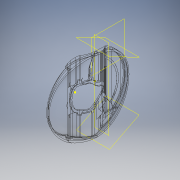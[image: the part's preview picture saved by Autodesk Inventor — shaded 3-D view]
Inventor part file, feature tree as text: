
AUTODESK INVENTOR PART (.ipt)
format: ipt  version: 2018 (Build 220112000, 112)  size: 2,382,336 bytes
history: native  units: mm
features: sketch x65, extrude x58, fillet x14, plane x4, revolve x1, mirror x1
ambient origin geometry x8: Origin, YZ Plane, XZ Plane, XY Plane, X Axis, Y Axis, Z Axis, Center Point
bodies: Solid1 (feature_tree)
feature tree (143):
  extrude  "Extrusion1"  TaperAngle=0.0deg  [1 undecoded]
  extrude  "Extrusion2"  Depth=10.0mm TaperAngle=0.0deg
  extrude  "Extrusion3"  Depth=10.0mm
  extrude  "Extrusion4"  TaperAngle=0.0deg  [1 undecoded]
  extrude  "Extrusion5"  Depth=10.0mm TaperAngle=0.0deg
  sketch  "Sketch6"  dims[d19=10.0mm d20=0.0mm d21=40.0mm]
  extrude  "Extrusion6"  Depth=10.0mm
  extrude  "Extrusion7"  Depth=11.0mm TaperAngle=0.0deg
  extrude  "Extrusion8"  Depth=32.0mm TaperAngle=0.0deg
  extrude  "Extrusion9"  Depth=32.0mm TaperAngle=0.0deg
  extrude  "Extrusion10"  Depth=10.0mm TaperAngle=0.0deg
  extrude  "Extrusion11"  Depth=10.0mm TaperAngle=0.0deg
  extrude  "Extrusion12"  TaperAngle=0.0deg  [1 undecoded]
  extrude  "Extrusion14"  Depth=48.3mm
  extrude  "Extrusion15"  TaperAngle=0.0deg  [1 undecoded]
  extrude  "Extrusion16"  Depth=10.0mm TaperAngle=0.0deg
  extrude  "Extrusion17"  Depth=11.63mm TaperAngle=0.0deg
  sketch  "Sketch21"  dims[d83=0.0mm d84=0.0mm d85=0.0mm d86=0.0mm]
  extrude  "Extrusion19"  Depth=11.63mm TaperAngle=0.0deg
  extrude  "Extrusion20"  TaperAngle=0.0deg  [1 undecoded]
  extrude  "Extrusion21"  Depth=10.0mm TaperAngle=0.0deg
  extrude  "Extrusion22"  TaperAngle=0.0deg  [1 undecoded]
  extrude  "Extrusion23"  Depth=2.86mm TaperAngle=0.0deg
  extrude  "Extrusion24"  TaperAngle=0.0deg  [1 undecoded]
  extrude  "Extrusion25"  Depth=2.22mm
  sketch  "Sketch33"  dims[d113=7.8mm d114=0.0mm d115=7.8mm d116=0.0mm]
  extrude  "Extrusion26"  Depth=10.0mm TaperAngle=0.0deg
  extrude  "Extrusion27"  Depth=7.8mm TaperAngle=0.0deg
  extrude  "Extrusion28"  Depth=16.0mm TaperAngle=0.0deg
  extrude  "Extrusion29"  Depth=22.0mm TaperAngle=0.0deg
  extrude  "Extrusion30"  Depth=17.0mm TaperAngle=0.0deg
  extrude  "Extrusion31"  Depth=2.0mm
  extrude  "Extrusion32"  Depth=2.0mm TaperAngle=0.0deg
  extrude  "Extrusion33"  Depth=18.0mm TaperAngle=0.0deg
  sketch  "Sketch42"  dims[d145=2.0mm d146=7.72mm d147=0.0mm]
  extrude  "Extrusion34"  Depth=16.0mm
  extrude  "Extrusion36"  Depth=15.5mm TaperAngle=0.0deg
  extrude  "Extrusion37"  Depth=2.0mm TaperAngle=0.0deg
  revolve  "Revolution3"  [1 undecoded]
  extrude  "Extrusion38"  Depth=2.0mm
  extrude  "Extrusion39"  Depth=2.0mm
  extrude  "Extrusion40"  Depth=2.0mm
  fillet  "Fillet1"  Radius=2.0mm
  fillet  "Fillet2"  Radius=10.0mm
  sketch  "Sketch51"
  extrude  "Extrusion41"  Depth=20.0mm TaperAngle=0.0deg
  mirror  "Mirror1"
  extrude  "Extrusion42"  [1 undecoded]
  sketch  "Sketch54"
  sketch  "Sketch55"
  sketch  "Sketch56"
  extrude  "Extrusion44"  [1 undecoded]
  extrude  "Extrusion45"  [1 undecoded]
  extrude  "Extrusion46"  [1 undecoded]
  extrude  "Extrusion47"  [1 undecoded]
  plane  "Work Plane2"
  extrude  "Extrusion48"  [1 undecoded]
  extrude  "Extrusion49"  [1 undecoded]
  plane  "Work Plane4"
  sketch  "Sketch64"
  plane  "Work Plane5"
  extrude  "Extrusion50"  [1 undecoded]
  extrude  "Extrusion51"  [1 undecoded]
  fillet  "Fillet3"  [1 undecoded]
  fillet  "Fillet4"  [1 undecoded]
  extrude  "Extrusion52"  [1 undecoded]
  extrude  "Extrusion53"  [1 undecoded]
  extrude  "Extrusion54"  [1 undecoded]
  extrude  "Extrusion55"  [1 undecoded]
  fillet  "Fillet5"  [1 undecoded]
  extrude  "Extrusion56"  [1 undecoded]
  extrude  "Extrusion57"  [1 undecoded]
  fillet  "Fillet6"  [1 undecoded]
  extrude  "Extrusion58"  [1 undecoded]
  extrude  "Extrusion59"  [1 undecoded]
  fillet  "Fillet7"  [1 undecoded]
  fillet  "Fillet8"  [1 undecoded]
  fillet  "Fillet9"  [1 undecoded]
  fillet  "Fillet10"  [1 undecoded]
  fillet  "Fillet11"  [1 undecoded]
  fillet  "Fillet12"  [1 undecoded]
  fillet  "Fillet13"  [1 undecoded]
  fillet  "Fillet14"  [1 undecoded]
  extrude  "Extrusion60"  [1 undecoded]
  extrude  "Extrusion61"  [1 undecoded]
  extrude  "Extrusion62"  [1 undecoded]
  sketch  "Sketch1"  dims[d0=10.0mm d1=0.0mm d2=0.0mm d3=0.0mm]
  sketch  "Sketch2"  dims[d4=0.0mm d5=0.0mm d6=10.0mm d7=0.0mm]
  sketch  "Sketch3"  dims[d8=10.0mm d9=0.0mm d10=50.0mm]
  sketch  "Sketch4"  dims[d11=10.0mm d12=0.0mm d13=0.0mm d14=0.0mm]
  sketch  "Sketch5"  dims[d15=0.0mm d16=0.0mm d17=10.0mm d18=0.0mm]
  sketch  "Sketch7"  dims[d22=38.0mm d23=11.0mm d24=0.0mm]
  sketch  "Sketch8"  dims[d25=9.5mm d26=0.0mm d33=32.0mm d34=0.0mm]
  sketch  "Sketch9"  dims[d37=32.0mm d38=0.0mm d39=32.0mm d40=0.0mm]
  sketch  "Sketch10"  dims[d41=32.0mm d42=0.0mm d45=10.0mm d46=0.0mm]
  sketch  "Sketch11"  dims[d47=10.0mm d48=0.0mm d49=10.0mm d50=0.0mm]
  sketch  "Sketch12"  dims[d51=0.0mm d52=0.0mm d53=0.0mm d54=0.0mm]
  sketch  "Sketch13"  dims[d65=46.0mm d66=48.3mm]
  sketch  "Sketch16"  dims[d67=9.0mm d68=0.0mm d69=0.0mm d70=0.0mm]
  sketch  "Sketch18"  dims[d71=0.0mm d72=0.0mm d73=10.0mm d74=0.0mm]
  sketch  "Sketch19"  dims[d75=5.0mm d76=0.0mm d77=11.63mm d78=0.0mm]
  sketch  "Sketch20"  dims[d79=11.63mm d80=0.0mm d81=11.63mm d82=0.0mm]
  sketch  "Sketch22"  dims[d87=30.0mm d88=10.0mm d89=0.0mm]
  sketch  "Sketch23"  dims[d92=10.0mm d93=0.0mm d94=0.0mm d95=0.0mm]
  sketch  "Sketch24"  dims[d96=135.0deg d99=2.86mm d100=0.0mm]
  sketch  "Sketch25"  dims[d101=0.0mm d102=0.0mm d103=0.0mm d104=0.0mm]
  sketch  "Sketch31"  dims[d105=2.01mm d106=2.22mm]
  sketch  "Sketch32"  dims[d107=10.0mm d108=0.0mm d109=10.0mm d110=0.0mm]
  sketch  "Sketch34"  dims[d117=0.0mm d118=0.0mm d119=16.0mm d120=0.0mm]
  sketch  "Sketch35"  dims[d121=22.0mm d122=0.0mm d123=22.0mm d124=0.0mm]
  sketch  "Sketch36"  dims[d125=90.0deg d126=17.0mm d127=0.0mm]
  sketch  "Sketch37"  dims[d128=17.0mm d129=0.0mm d130=2.0mm]
  sketch  "Sketch38"  dims[d131=2.0mm d132=6.95mm d133=0.0mm]
  sketch  "Sketch39"  dims[d134=6.95mm d135=0.0mm d136=18.0mm d137=0.0mm]
  sketch  "Sketch40"  dims[d138=16.0mm d139=0.0mm d140=1.02mm]
  sketch  "Sketch41"  dims[d141=1.0mm d142=0.0mm d143=15.5mm d144=0.0mm]
  sketch  "Sketch43"  dims[d148=17.0mm d149=0.0mm d150=2.0mm]
  sketch  "Sketch45"  dims[d151=2.0mm d152=2.0mm]
  sketch  "Sketch47"  dims[d153=2.0mm d154=2.0mm]
  sketch  "Sketch48"  dims[d155=2.0mm d156=2.0mm d157=2.0mm d158=10.0mm d159=0.0mm]
  sketch  "Sketch49"  dims[d160=7.83mm d161=0.0mm d162=20.0mm d163=0.0mm]
  sketch  "Sketch50"
  sketch  "Sketch52"
  sketch  "Sketch53"
  sketch  "Sketch57"
  sketch  "Sketch60"
  sketch  "Sketch61"
  sketch  "Sketch62"
  sketch  "Sketch63"
  plane  "Work Plane3"
  sketch  "Sketch65"
  sketch  "Sketch66"
  sketch  "Sketch67"
  sketch  "Sketch68"
  sketch  "Sketch69"
  sketch  "Sketch70"
  sketch  "Sketch71"
  sketch  "Sketch72"
  sketch  "Sketch73"
  sketch  "Sketch74"
  sketch  "Sketch75"
  sketch  "Sketch76"
  sketch  "Sketch78"
note: 40 required parameter values undecoded (feature->parameter linkage not recoverable at this tier; creation-order binding heuristic only, values carry confidence <= 0.55)